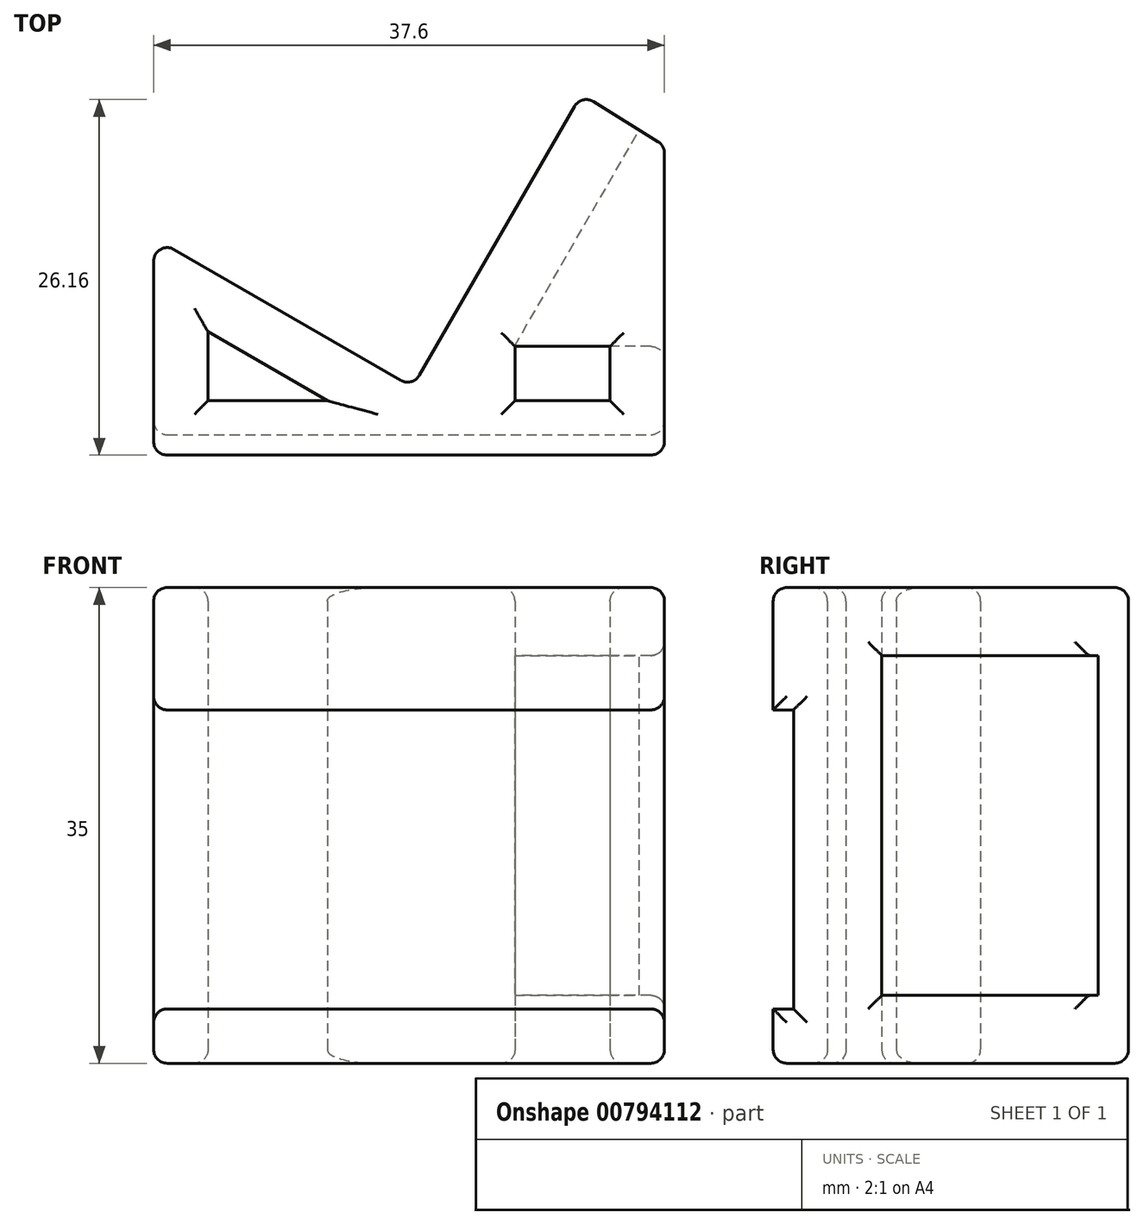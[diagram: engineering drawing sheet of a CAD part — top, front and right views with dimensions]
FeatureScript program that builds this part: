
annotation { "Feature Type Name" : "Feature", "Feature Type Description" : "" }
export const myFeature = defineFeature(function(context is Context, id is Id, definition is map)
    precondition{}
    {
        {
            var Q0;
            Q0=qCreatedBy(makeId("Top.planeOp"),FACE);
            var sketch = newSketch(context, id + "F0", { "sketchPlane" : qUnion([Q0])});
            skLineSegment(sketch, "E0", {"start": v(-24.6, -5) * mm, "end": v(13, -5) * mm});
            skLineSegment(sketch, "E1", {"start": v(13, -5) * mm, "end": v(13, 17.77) * mm});
            skLineSegment(sketch, "E2", {"start": v(-5.54, 0) * mm, "end": v(-24.6, 11) * mm});
            skLineSegment(sketch, "E3", {"start": v(-24.6, 11) * mm, "end": v(-24.6, -5) * mm});
            skLineSegment(sketch, "E4", {"start": v(-24.6, 0) * mm, "end": v(13, 0) * mm, "construction": true});
            skLineSegment(sketch, "E5.bottom", {"start": v(2, 3) * mm, "end": v(9, 3) * mm});
            skLineSegment(sketch, "E5.top", {"start": v(2, -1) * mm, "end": v(9, -1) * mm});
            skLineSegment(sketch, "E5.left", {"start": v(2, 3) * mm, "end": v(2, -1) * mm});
            skLineSegment(sketch, "E5.right", {"start": v(9, 3) * mm, "end": v(9, -1) * mm});
            skLineSegment(sketch, "E6", {"start": v(-20.6, 4.07) * mm, "end": v(-20.6, -1) * mm});
            skLineSegment(sketch, "E7", {"start": v(-20.6, -1) * mm, "end": v(-11.81, -1) * mm});
            skLineSegment(sketch, "E8", {"start": v(-11.81, -1) * mm, "end": v(-20.6, 4.07) * mm});
            skLineSegment(sketch, "E9", {"start": v(-5.54, 0) * mm, "end": v(6.9, 21.55) * mm});
            skLineSegment(sketch, "E10", {"start": v(6.9, 21.55) * mm, "end": v(13, 17.77) * mm});
            skSolve(sketch);
        }
        {
            var Q0;
            Q0=makeQuery(id+"F0.imprint","IMPRINT",FACE,{"disambiguationData":[TD([[makeQuery(id+"F0.imprint","IMPRINT",EDGE,{"derivedFrom":sQuery(id+"F0.wireOp",EDGE,"E0")}),1.0]])]});
            extrude(context, id + "F1", {"entities" : qUnion([Q0]), "depth" : 35 * mm, "offsetDistance" : 25 * mm});
        }
        {
            var Q0;
            Q0=makeQuery(id+"F1.opExtrude","SWEPT_FACE",FACE,{"disambiguationData":[OSD([sQuery(id+"F0.wireOp",EDGE,"E0")])]});
            var sketch = newSketch(context, id + "F2", { "sketchPlane" : qUnion([Q0])});
            skLineSegment(sketch, "E11", {"start": v(-24.6, 26) * mm, "end": v(13, 26) * mm});
            skLineSegment(sketch, "E12", {"start": v(13, 26) * mm, "end": v(13, 4) * mm});
            skLineSegment(sketch, "E13", {"start": v(13, 4) * mm, "end": v(-24.6, 4) * mm});
            skLineSegment(sketch, "E14", {"start": v(-24.6, 4) * mm, "end": v(-24.6, 26) * mm});
            skSolve(sketch);
        }
        {
            var Q0;
            Q0=makeQuery(id+"F1.opExtrude","CAP_FACE",FACE,{"disambiguationData":[OSD([sQuery(id+"F0.wireOp",EDGE,"E0"),sQuery(id+"F0.wireOp",EDGE,"E1"),sQuery(id+"F0.wireOp",EDGE,"E2"),sQuery(id+"F0.wireOp",EDGE,"E3"),sQuery(id+"F0.wireOp",EDGE,"E5.bottom"),sQuery(id+"F0.wireOp",EDGE,"E5.top"),sQuery(id+"F0.wireOp",EDGE,"E5.left"),sQuery(id+"F0.wireOp",EDGE,"E5.right"),sQuery(id+"F0.wireOp",EDGE,"E6"),sQuery(id+"F0.wireOp",EDGE,"E7"),sQuery(id+"F0.wireOp",EDGE,"E8"),sQuery(id+"F0.wireOp",EDGE,"E9"),sQuery(id+"F0.wireOp",EDGE,"E10")])],"isStart":true});
            cPlane(context, id + "F3", {"entities" : qUnion([Q0]), "cplaneType" : CPlaneType.OFFSET, "offset" : 5 * mm, "oppositeDirection" : true, "width" : 150 * mm, "height" : 150 * mm});
        }
        {
            var Q0;
            Q0=qCreatedBy(id+"F3.planeOp",FACE);
            var sketch = newSketch(context, id + "F4", { "sketchPlane" : qUnion([Q0])});
            skLineSegment(sketch, "E15", {"start": v(13, -3) * mm, "end": v(1.96, -3) * mm});
            skLineSegment(sketch, "E16", {"start": v(1.96, -3) * mm, "end": v(13, -22.13) * mm});
            skLineSegment(sketch, "E17", {"start": v(13, -3) * mm, "end": v(13, -22.13) * mm});
            skSolve(sketch);
        }
        {
            var Q0;
            Q0=makeQuery(id+"F4.imprint","IMPRINT",FACE,{"disambiguationData":[TD([[makeQuery(id+"F4.imprint","IMPRINT",EDGE,{"derivedFrom":sQuery(id+"F4.wireOp",EDGE,"E15")}),1.0]])]});
            extrude(context, id + "F5", {"entities" : qUnion([Q0]), "operationType" : NewBodyOperationType.REMOVE, "oppositeDirection" : true, "depth" : 25 * mm, "offsetDistance" : 25 * mm});
        }
        {
            var Q0;
            Q0=makeQuery(id+"F2.imprint","IMPRINT",FACE,{"disambiguationData":[TD([[makeQuery(id+"F2.imprint","IMPRINT",EDGE,{"derivedFrom":sQuery(id+"F2.wireOp",EDGE,"E11")}),-1.0]])]});
            extrude(context, id + "F6", {"entities" : qUnion([Q0]), "operationType" : NewBodyOperationType.REMOVE, "oppositeDirection" : true, "depth" : 1.5 * mm, "offsetDistance" : 25 * mm});
        }
        {
            var Q0;
            Q0=makeQuery(id+"F1.opExtrude","SWEPT_FACE",FACE,{"disambiguationData":[OSD([sQuery(id+"F0.wireOp",EDGE,"E9")])]});
            var Q1;
            Q1=makeQuery(id+"F1.opExtrude","SWEPT_FACE",FACE,{"disambiguationData":[OSD([sQuery(id+"F0.wireOp",EDGE,"E2")])]});
            var Q2;
            Q2=makeQuery(id+"F1.opExtrude","CAP_FACE",FACE,{"disambiguationData":[OSD([sQuery(id+"F0.wireOp",EDGE,"E0"),sQuery(id+"F0.wireOp",EDGE,"E1"),sQuery(id+"F0.wireOp",EDGE,"E2"),sQuery(id+"F0.wireOp",EDGE,"E3"),sQuery(id+"F0.wireOp",EDGE,"E5.bottom"),sQuery(id+"F0.wireOp",EDGE,"E5.top"),sQuery(id+"F0.wireOp",EDGE,"E5.left"),sQuery(id+"F0.wireOp",EDGE,"E5.right"),sQuery(id+"F0.wireOp",EDGE,"E6"),sQuery(id+"F0.wireOp",EDGE,"E7"),sQuery(id+"F0.wireOp",EDGE,"E8"),sQuery(id+"F0.wireOp",EDGE,"E9"),sQuery(id+"F0.wireOp",EDGE,"E10")])],"isStart":true});
            var Q3;
            Q3=makeQuery(id+"F1.opExtrude","SWEPT_FACE",FACE,{"disambiguationData":[OSD([sQuery(id+"F0.wireOp",EDGE,"E3")])]});
            var Q4;
            Q4=makeQuery(id+"F1.opExtrude","CAP_FACE",FACE,{"disambiguationData":[OSD([sQuery(id+"F0.wireOp",EDGE,"E0"),sQuery(id+"F0.wireOp",EDGE,"E1"),sQuery(id+"F0.wireOp",EDGE,"E2"),sQuery(id+"F0.wireOp",EDGE,"E3"),sQuery(id+"F0.wireOp",EDGE,"E5.bottom"),sQuery(id+"F0.wireOp",EDGE,"E5.top"),sQuery(id+"F0.wireOp",EDGE,"E5.left"),sQuery(id+"F0.wireOp",EDGE,"E5.right"),sQuery(id+"F0.wireOp",EDGE,"E6"),sQuery(id+"F0.wireOp",EDGE,"E7"),sQuery(id+"F0.wireOp",EDGE,"E8"),sQuery(id+"F0.wireOp",EDGE,"E9"),sQuery(id+"F0.wireOp",EDGE,"E10")])],"isStart":false});
            var Q5;
            Q5=makeQuery(id+"F1.opExtrude","SWEPT_FACE",FACE,{"disambiguationData":[OSD([sQuery(id+"F0.wireOp",EDGE,"E1")])]});
            fillet(context, id + "F7", {"entities" : qUnion([Q0, Q1, Q2, Q3, Q4, Q5]), "radius" : 1 * mm, "tangentPropagation" : true, "allowEdgeOverflow" : false});
        }
    });
